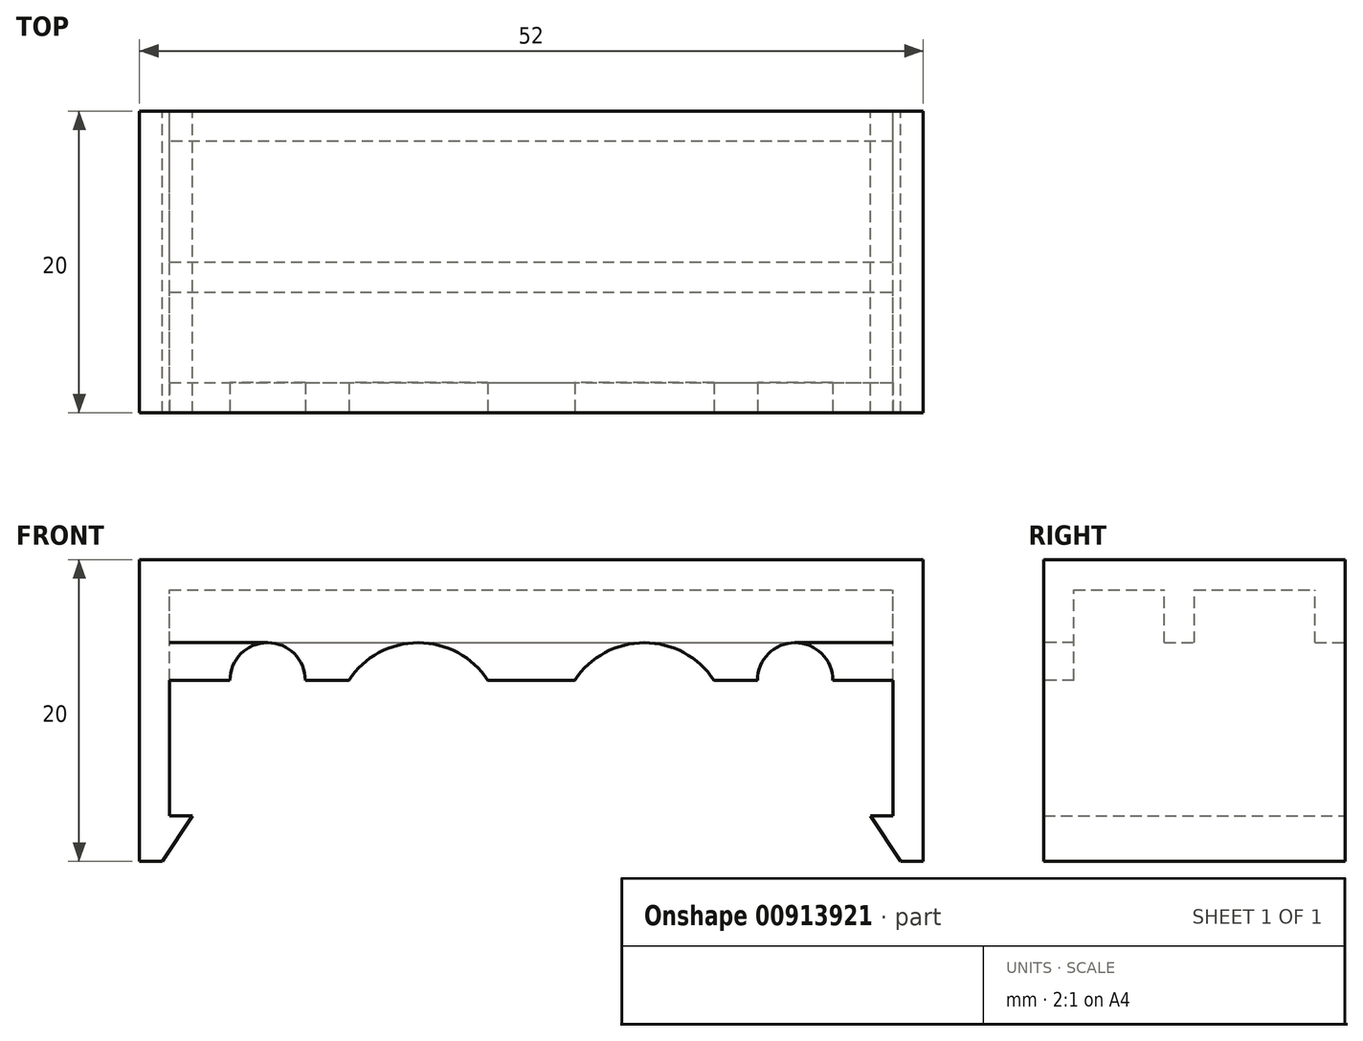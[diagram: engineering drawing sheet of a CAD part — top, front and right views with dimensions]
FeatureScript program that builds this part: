
annotation { "Feature Type Name" : "Feature", "Feature Type Description" : "" }
export const myFeature = defineFeature(function(context is Context, id is Id, definition is map)
    precondition{}
    {
        {
            var Q0;
            Q0=qCreatedBy(makeId("Front.planeOp"),FACE);
            var sketch = newSketch(context, id + "F0", { "sketchPlane" : qUnion([Q0])});
            skLineSegment(sketch, "E0", {"start": v(26, 12.43) * mm, "end": v(26, -7.57) * mm});
            skLineSegment(sketch, "E1", {"start": v(26, -7.57) * mm, "end": v(24.5, -7.57) * mm});
            skLineSegment(sketch, "E2", {"start": v(24.5, -7.57) * mm, "end": v(22.5, -4.57) * mm});
            skLineSegment(sketch, "E3", {"start": v(22.5, -4.57) * mm, "end": v(24, -4.57) * mm});
            skLineSegment(sketch, "E4", {"start": v(24, -4.57) * mm, "end": v(24, 10.43) * mm});
            skPoint(sketch, "E5.start.orphan", {"position": v(-25.07, 0) * mm});
            skLineSegment(sketch, "E6.MirrorCS", {"start": v(-26, -7.57) * mm, "end": v(-24.5, -7.57) * mm});
            skLineSegment(sketch, "E7.MirrorCS", {"start": v(-24.5, -7.57) * mm, "end": v(-22.5, -4.57) * mm});
            skLineSegment(sketch, "E8.MirrorCS", {"start": v(-22.5, -4.57) * mm, "end": v(-24, -4.57) * mm});
            skLineSegment(sketch, "E9.MirrorCS", {"start": v(-26, 12.43) * mm, "end": v(-26, -7.57) * mm});
            skLineSegment(sketch, "E10.MirrorCS", {"start": v(-24, -4.57) * mm, "end": v(-24, 10.43) * mm});
            skLineSegment(sketch, "E11", {"start": v(-26, 12.43) * mm, "end": v(26, 12.43) * mm});
            skLineSegment(sketch, "E12", {"start": v(-24, 10.43) * mm, "end": v(24, 10.43) * mm});
            skSolve(sketch);
        }
        {
            var Q0;
            Q0 = qSketchRegion(id + "F0", true);
            extrude(context, id + "F1", {"entities" : qUnion([Q0]), "depth" : 20 * mm, "offsetDistance" : 25 * mm});
        }
        {
            var Q0;
            Q0=makeQuery(id+"F1.opExtrude","SWEPT_FACE",FACE,{"disambiguationData":[OSD([sQuery(id+"F0.wireOp",EDGE,"E12")])]});
            var sketch = newSketch(context, id + "F2", { "sketchPlane" : qUnion([Q0])});
            skLineSegment(sketch, "E13.bottom", {"start": v(24, 2) * mm, "end": v(-24, 2) * mm});
            skLineSegment(sketch, "E13.top", {"start": v(24, 0) * mm, "end": v(-24, 0) * mm});
            skLineSegment(sketch, "E13.left", {"start": v(24, 2) * mm, "end": v(24, 0) * mm});
            skLineSegment(sketch, "E13.right", {"start": v(-24, 2) * mm, "end": v(-24, 0) * mm});
            skLineSegment(sketch, "E14.bottom", {"start": v(-24, 12) * mm, "end": v(24, 12) * mm});
            skLineSegment(sketch, "E14.top", {"start": v(-24, 10) * mm, "end": v(24, 10) * mm});
            skLineSegment(sketch, "E14.left", {"start": v(-24, 12) * mm, "end": v(-24, 10) * mm});
            skLineSegment(sketch, "E14.right", {"start": v(24, 12) * mm, "end": v(24, 10) * mm});
            skSolve(sketch);
        }
        {
            var Q0;
            Q0 = qSketchRegion(id + "F2", true);
            extrude(context, id + "F3", {"entities" : qUnion([Q0]), "operationType" : NewBodyOperationType.ADD, "depth" : 3.5 * mm, "offsetDistance" : 25 * mm});
        }
        {
            var Q0;
            Q0=makeQuery(id+"F1.opExtrude","CAP_FACE",FACE,{"disambiguationData":[OSD([sQuery(id+"F0.wireOp",EDGE,"E0"),sQuery(id+"F0.wireOp",EDGE,"E1"),sQuery(id+"F0.wireOp",EDGE,"E2"),sQuery(id+"F0.wireOp",EDGE,"E3"),sQuery(id+"F0.wireOp",EDGE,"E4"),sQuery(id+"F0.wireOp",EDGE,"E6.MirrorCS"),sQuery(id+"F0.wireOp",EDGE,"E7.MirrorCS"),sQuery(id+"F0.wireOp",EDGE,"E8.MirrorCS"),sQuery(id+"F0.wireOp",EDGE,"E9.MirrorCS"),sQuery(id+"F0.wireOp",EDGE,"E10.MirrorCS"),sQuery(id+"F0.wireOp",EDGE,"E11"),sQuery(id+"F0.wireOp",EDGE,"E12")])],"isStart":false});
            var sketch = newSketch(context, id + "F4", { "sketchPlane" : qUnion([Q0])});
            skLineSegment(sketch, "E15.0", {"start": v(-26, 12.43) * mm, "end": v(26, 12.43) * mm});
            skLineSegment(sketch, "E16.0", {"start": v(-26, 12.43) * mm, "end": v(-26, 4.43) * mm});
            skLineSegment(sketch, "E17.0", {"start": v(26, 12.43) * mm, "end": v(26, 4.43) * mm});
            skArc(sketch, "E18", {"start": v(-2.9, 4.43) * mm, "mid": v(-7.5, 6.93) * mm, "end": v(-12.1, 4.43) * mm});
            skArc(sketch, "E19", {"start": v(-15, 4.43) * mm, "mid": v(-17.5, 6.93) * mm, "end": v(-20, 4.43) * mm});
            skArc(sketch, "E20.MirrorC", {"start": v(2.9, 4.43) * mm, "mid": v(7.5, 6.93) * mm, "end": v(12.1, 4.43) * mm});
            skArc(sketch, "E21.MirrorC", {"start": v(15, 4.43) * mm, "mid": v(17.5, 6.93) * mm, "end": v(20, 4.43) * mm});
            skLineSegment(sketch, "E22", {"start": v(-26, 4.43) * mm, "end": v(-20, 4.43) * mm});
            skPoint(sketch, "E23.orphan", {"position": v(26, -7.57) * mm});
            skPoint(sketch, "E24.orphan", {"position": v(-26, -7.57) * mm});
            skLineSegment(sketch, "E25.trimOffspring", {"start": v(-15, 4.43) * mm, "end": v(-12.1, 4.43) * mm});
            skLineSegment(sketch, "E26.trimOffspring", {"start": v(-2.9, 4.43) * mm, "end": v(2.9, 4.43) * mm});
            skLineSegment(sketch, "E27.trimOffspring", {"start": v(12.1, 4.43) * mm, "end": v(15, 4.43) * mm});
            skLineSegment(sketch, "E28.trimOffspring", {"start": v(20, 4.43) * mm, "end": v(26, 4.43) * mm});
            skSolve(sketch);
        }
        {
            var Q0;
            Q0 = qSketchRegion(id + "F4", true);
            extrude(context, id + "F5", {"entities" : qUnion([Q0]), "operationType" : NewBodyOperationType.ADD, "oppositeDirection" : true, "depth" : 2 * mm, "offsetDistance" : 25 * mm});
        }
    });
